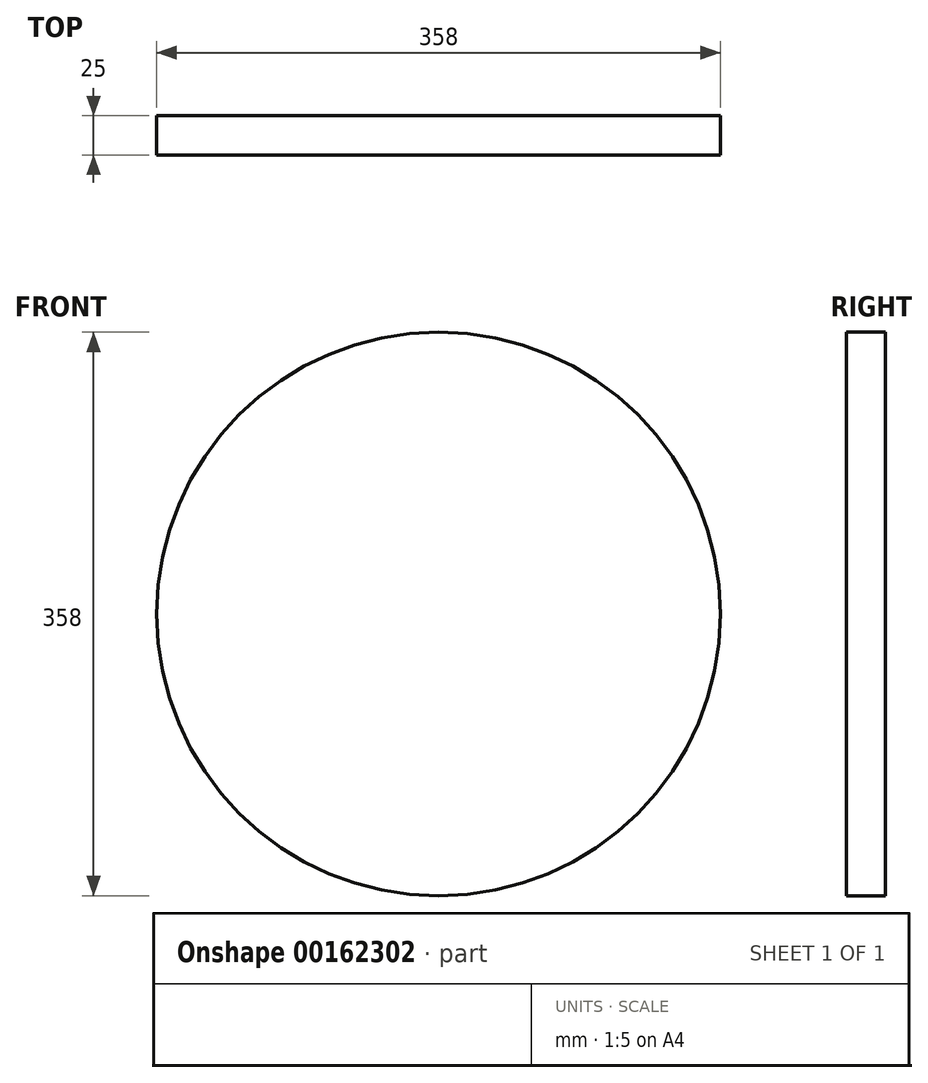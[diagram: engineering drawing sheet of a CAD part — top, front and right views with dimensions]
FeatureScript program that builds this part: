
annotation { "Feature Type Name" : "Feature", "Feature Type Description" : "" }
export const myFeature = defineFeature(function(context is Context, id is Id, definition is map)
    precondition{}
    {
        {
            var Q0;
            Q0=qCreatedBy(makeId("Front.planeOp"),FACE);
            var sketch = newSketch(context, id + "F0", { "sketchPlane" : qUnion([Q0])});
            skCircle(sketch, "E0", {"center": v(0, 0) * mm, "radius": 179 * mm});
            skSolve(sketch);
        }
        {
            var Q0;
            Q0 = qSketchRegion(id + "F0", true);
            extrude(context, id + "F1", {"entities" : qUnion([Q0]), "depth" : 25 * mm});
        }
    });
